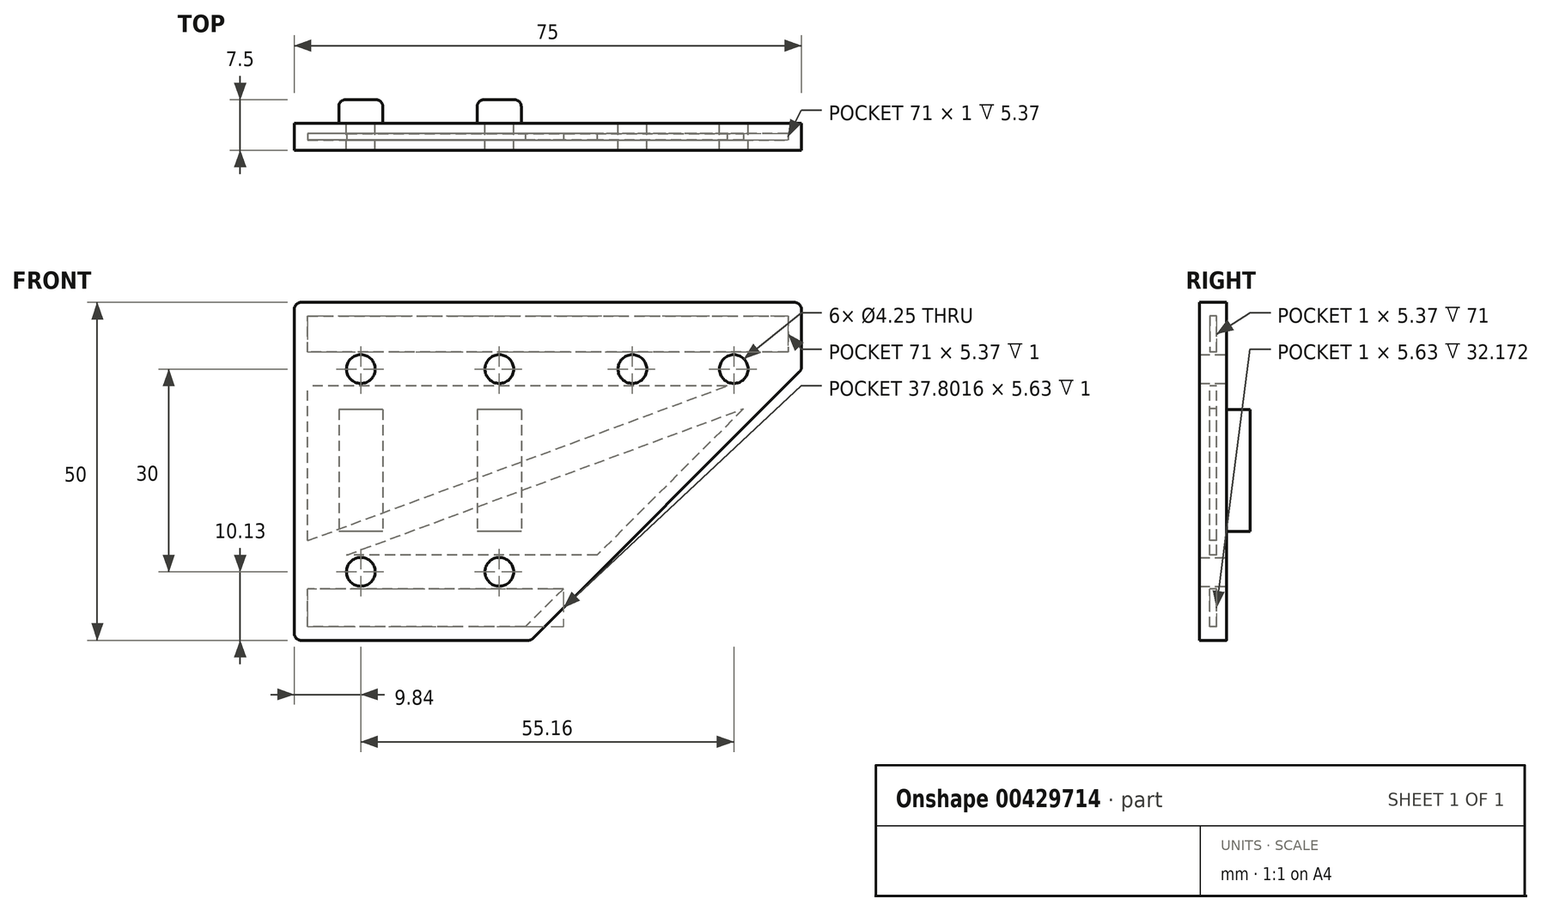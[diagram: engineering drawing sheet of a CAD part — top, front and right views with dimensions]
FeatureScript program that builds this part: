
annotation { "Feature Type Name" : "Feature", "Feature Type Description" : "" }
export const myFeature = defineFeature(function(context is Context, id is Id, definition is map)
    precondition{}
    {
        {
            var Q0;
            Q0=qCreatedBy(makeId("Front.planeOp"),FACE);
            var sketch = newSketch(context, id + "F0", { "sketchPlane" : qUnion([Q0])});
            skLineSegment(sketch, "E0", {"start": v(0, 0) * mm, "end": v(0, 50) * mm});
            skLineSegment(sketch, "E1", {"start": v(0, 50) * mm, "end": v(75, 50) * mm});
            skLineSegment(sketch, "E2", {"start": v(75, 50) * mm, "end": v(75, 40) * mm});
            skLineSegment(sketch, "E3", {"start": v(75, 40) * mm, "end": v(35, 0) * mm});
            skLineSegment(sketch, "E4", {"start": v(35, 0) * mm, "end": v(0, 0) * mm});
            skSolve(sketch);
        }
        {
            var Q0;
            Q0 = qSketchRegion(id + "F0", true);
            extrude(context, id + "F1", {"entities" : qUnion([Q0]), "depth" : 1.5 * mm});
        }
        {
            var Q0;
            Q0=makeQuery(id+"F1.opExtrude","CAP_FACE",FACE,{"disambiguationData":[OSD([sQuery(id+"F0.wireOp",EDGE,"E0"),sQuery(id+"F0.wireOp",EDGE,"E1"),sQuery(id+"F0.wireOp",EDGE,"E2"),sQuery(id+"F0.wireOp",EDGE,"E3"),sQuery(id+"F0.wireOp",EDGE,"E4")])],"isStart":true});
            var sketch = newSketch(context, id + "F2", { "sketchPlane" : qUnion([Q0])});
            skLineSegment(sketch, "E5", {"start": v(-73, 42.63) * mm, "end": v(-2, 42.63) * mm});
            skLineSegment(sketch, "E6", {"start": v(-64.02, 37.63) * mm, "end": v(-2, 37.63) * mm});
            skLineSegment(sketch, "E7.0", {"start": v(0, 50) * mm, "end": v(-75, 50) * mm});
            skLineSegment(sketch, "E8.0", {"start": v(0, 0) * mm, "end": v(0, 50) * mm});
            skLineSegment(sketch, "E9.0", {"start": v(-2, 2) * mm, "end": v(-2, 7.63) * mm});
            skLineSegment(sketch, "E9.1", {"start": v(-34.17, 2) * mm, "end": v(-2, 2) * mm});
            skLineSegment(sketch, "E9.2", {"start": v(-2, 48) * mm, "end": v(-73, 48) * mm});
            skLineSegment(sketch, "E9.3", {"start": v(-73, 48) * mm, "end": v(-73, 42.63) * mm});
            skLineSegment(sketch, "E9.4", {"start": v(-66.42, 34.25) * mm, "end": v(-44.8, 12.63) * mm});
            skLineSegment(sketch, "E10", {"start": v(-44.8, 12.63) * mm, "end": v(-7.78, 12.63) * mm});
            skLineSegment(sketch, "E11", {"start": v(-39.8, 7.63) * mm, "end": v(-2, 7.63) * mm});
            skLineSegment(sketch, "E12.trimOffspring", {"start": v(-2, 42.63) * mm, "end": v(-2, 48) * mm});
            skLineSegment(sketch, "E13.trimOffspring", {"start": v(-39.8, 7.63) * mm, "end": v(-34.17, 2) * mm});
            skLineSegment(sketch, "E14.trimOffspring", {"start": v(-2, 14.76) * mm, "end": v(-2, 37.63) * mm});
            skLineSegment(sketch, "E15", {"start": v(-2, 12.63) * mm, "end": v(-69.8, 37.63) * mm, "construction": true});
            skLineSegment(sketch, "E16.0", {"start": v(-2, 14.76) * mm, "end": v(-64.02, 37.63) * mm});
            skLineSegment(sketch, "E17.0", {"start": v(-7.78, 12.63) * mm, "end": v(-66.42, 34.25) * mm});
            skSolve(sketch);
        }
        {
            var Q0;
            Q0=makeQuery(id+"F2.imprint","IMPRINT",FACE,{"disambiguationData":[TD([[makeQuery(id+"F2.imprint","IMPRINT",EDGE,{"derivedFrom":sQuery(id+"F2.wireOp",EDGE,"E5")}),-1.0]])]});
            extrude(context, id + "F3", {"entities" : qUnion([Q0]), "operationType" : NewBodyOperationType.ADD, "depth" : 1 * mm});
        }
        {
            var Q0;
            Q0=makeQuery(id+"F3.opExtrude","CAP_FACE",FACE,{"disambiguationData":[OSD([sQuery(id+"F0.wireOp",EDGE,"E2"),sQuery(id+"F0.wireOp",EDGE,"E3"),sQuery(id+"F0.wireOp",EDGE,"E4"),sQuery(id+"F2.wireOp",EDGE,"E5"),sQuery(id+"F2.wireOp",EDGE,"E6"),sQuery(id+"F2.wireOp",EDGE,"E7.0"),sQuery(id+"F2.wireOp",EDGE,"E8.0"),sQuery(id+"F2.wireOp",EDGE,"E9.0"),sQuery(id+"F2.wireOp",EDGE,"E9.1"),sQuery(id+"F2.wireOp",EDGE,"E9.2"),sQuery(id+"F2.wireOp",EDGE,"E9.3"),sQuery(id+"F2.wireOp",EDGE,"E9.4"),sQuery(id+"F2.wireOp",EDGE,"E10"),sQuery(id+"F2.wireOp",EDGE,"E11"),sQuery(id+"F2.wireOp",EDGE,"E12.trimOffspring"),sQuery(id+"F2.wireOp",EDGE,"E13.trimOffspring"),sQuery(id+"F2.wireOp",EDGE,"E14.trimOffspring"),sQuery(id+"F2.wireOp",EDGE,"E16.0"),sQuery(id+"F2.wireOp",EDGE,"E17.0")])],"isStart":false});
            var sketch = newSketch(context, id + "F4", { "sketchPlane" : qUnion([Q0])});
            skLineSegment(sketch, "E18.0", {"start": v(0, 50) * mm, "end": v(-75, 50) * mm});
            skLineSegment(sketch, "E19.0", {"start": v(-75, 50) * mm, "end": v(-75, 40) * mm});
            skLineSegment(sketch, "E20.0", {"start": v(-75, 40) * mm, "end": v(-35, 0) * mm});
            skLineSegment(sketch, "E21.0", {"start": v(-35, 0) * mm, "end": v(0, 0) * mm});
            skLineSegment(sketch, "E22.0", {"start": v(0, 0) * mm, "end": v(0, 50) * mm});
            skSolve(sketch);
        }
        {
            var Q0;
            Q0 = qSketchRegion(id + "F4", true);
            extrude(context, id + "F5", {"entities" : qUnion([Q0]), "operationType" : NewBodyOperationType.ADD, "depth" : 1.5 * mm});
        }
        {
            var Q0;
            Q0=makeQuery(id+"F1.opExtrude","CAP_FACE",FACE,{"disambiguationData":[OSD([sQuery(id+"F0.wireOp",EDGE,"E0"),sQuery(id+"F0.wireOp",EDGE,"E1"),sQuery(id+"F0.wireOp",EDGE,"E2"),sQuery(id+"F0.wireOp",EDGE,"E3"),sQuery(id+"F0.wireOp",EDGE,"E4")])],"isStart":true});
            var sketch = newSketch(context, id + "F6", { "sketchPlane" : qUnion([Q0])});
            skLineSegment(sketch, "E23", {"start": v(-6.5, 50) * mm, "end": v(-6.5, 0) * mm, "construction": true});
            skLineSegment(sketch, "E24", {"start": v(-13.18, 50) * mm, "end": v(-13.18, 0) * mm, "construction": true});
            skCircle(sketch, "E25", {"center": v(-9.84, 40.13) * mm, "radius": 2.12 * mm});
            skCircle(sketch, "E26", {"center": v(-9.84, 10.13) * mm, "radius": 2.12 * mm});
            skCircle(sketch, "E27", {"center": v(-30.32, 40.13) * mm, "radius": 2.12 * mm});
            skCircle(sketch, "E28", {"center": v(-30.32, 10.13) * mm, "radius": 2.12 * mm});
            skCircle(sketch, "E29", {"center": v(-50, 40.13) * mm, "radius": 2.12 * mm});
            skCircle(sketch, "E30", {"center": v(-65, 40.13) * mm, "radius": 2.12 * mm});
            skLineSegment(sketch, "E31", {"start": v(-13.18, 40.13) * mm, "end": v(-6.5, 40.13) * mm, "construction": true});
            skLineSegment(sketch, "E32", {"start": v(-13.18, 43.2) * mm, "end": v(-49.26, 43.2) * mm, "construction": true});
            skLineSegment(sketch, "E33", {"start": v(-13.18, 40.13) * mm, "end": v(-39.87, 40.13) * mm, "construction": true});
            skLineSegment(sketch, "E34", {"start": v(-26.98, 40.13) * mm, "end": v(-26.98, 18.65) * mm, "construction": true});
            skLineSegment(sketch, "E35", {"start": v(-30.32, 40.13) * mm, "end": v(-30.32, 27.39) * mm, "construction": true});
            skSolve(sketch);
        }
        {
            var Q0;
            Q0 = qSketchRegion(id + "F6", true);
            extrude(context, id + "F7", {"entities" : qUnion([Q0]), "operationType" : NewBodyOperationType.REMOVE, "oppositeDirection" : true, "depth" : 25 * mm, "hasSecondDirection" : true, "secondDirectionOppositeDirection" : false, "secondDirectionDepth" : 25 * mm});
        }
        {
            var Q0;
            Q0=makeQuery(id+"F5.opExtrude","CAP_FACE",FACE,{"disambiguationData":[OSD([sQuery(id+"F4.wireOp",EDGE,"E18.0"),sQuery(id+"F4.wireOp",EDGE,"E19.0"),sQuery(id+"F4.wireOp",EDGE,"E20.0"),sQuery(id+"F4.wireOp",EDGE,"E21.0"),sQuery(id+"F4.wireOp",EDGE,"E22.0")])],"isStart":false});
            var sketch = newSketch(context, id + "F8", { "sketchPlane" : qUnion([Q0])});
            skLineSegment(sketch, "E36.bottom", {"start": v(-13.1, 34.13) * mm, "end": v(-6.6, 34.13) * mm});
            skLineSegment(sketch, "E36.top", {"start": v(-13.1, 16.13) * mm, "end": v(-6.6, 16.13) * mm});
            skLineSegment(sketch, "E36.left", {"start": v(-13.1, 34.13) * mm, "end": v(-13.1, 16.13) * mm});
            skLineSegment(sketch, "E36.right", {"start": v(-6.6, 34.13) * mm, "end": v(-6.6, 16.13) * mm});
            skLineSegment(sketch, "E37", {"start": v(-9.84, 34.13) * mm, "end": v(-9.84, 30.86) * mm, "construction": true});
            skPoint(sketch, "E37.endSnap0", {"position": v(-9.84, 34.13) * mm});
            skLineSegment(sketch, "E38", {"start": v(-9.84, 39.13) * mm, "end": v(-9.84, 34.13) * mm, "construction": true});
            skLineSegment(sketch, "E39", {"start": v(-9.84, 11.13) * mm, "end": v(-9.84, 16.13) * mm, "construction": true});
            skLineSegment(sketch, "E40.bottom", {"start": v(-33.57, 34.13) * mm, "end": v(-27.07, 34.13) * mm});
            skLineSegment(sketch, "E40.top", {"start": v(-33.57, 16.13) * mm, "end": v(-27.07, 16.13) * mm});
            skLineSegment(sketch, "E40.left", {"start": v(-33.57, 34.13) * mm, "end": v(-33.57, 16.13) * mm});
            skLineSegment(sketch, "E40.right", {"start": v(-27.07, 34.13) * mm, "end": v(-27.07, 16.13) * mm});
            skLineSegment(sketch, "E41", {"start": v(-30.32, 16.13) * mm, "end": v(-30.32, 17.83) * mm, "construction": true});
            skSolve(sketch);
        }
        {
            var Q0;
            Q0 = qSketchRegion(id + "F8", true);
            extrude(context, id + "F9", {"entities" : qUnion([Q0]), "operationType" : NewBodyOperationType.ADD, "depth" : 3.5 * mm});
        }
        {
            var Q0;
            Q0=makeQuery(id+"F9.opExtrude","CAP_EDGE",EDGE,{"disambiguationData":[OSD([sQuery(id+"F8.wireOp",EDGE,"E40.left")])],"isStart":false});
            var Q1;
            Q1=makeQuery(id+"F9.opExtrude","CAP_EDGE",EDGE,{"disambiguationData":[OSD([sQuery(id+"F8.wireOp",EDGE,"E40.right")])],"isStart":false});
            var Q2;
            Q2=makeQuery(id+"F9.opExtrude","CAP_EDGE",EDGE,{"disambiguationData":[OSD([sQuery(id+"F8.wireOp",EDGE,"E36.left")])],"isStart":false});
            var Q3;
            Q3=makeQuery(id+"F9.opExtrude","CAP_EDGE",EDGE,{"disambiguationData":[OSD([sQuery(id+"F8.wireOp",EDGE,"E36.right")])],"isStart":false});
            var Q4;
            Q4=makeQuery(id+"F1.opExtrude","SWEPT_EDGE",EDGE,{"disambiguationData":[OSD([sQuery(id+"F0.wireOp",EDGE,"E0"),sQuery(id+"F0.wireOp",EDGE,"E1")])]});
            var Q5;
            Q5=makeQuery(id+"F1.opExtrude","SWEPT_EDGE",EDGE,{"disambiguationData":[OSD([sQuery(id+"F0.wireOp",EDGE,"E0"),sQuery(id+"F0.wireOp",EDGE,"E4")])]});
            var Q6;
            Q6=makeQuery(id+"F1.opExtrude","SWEPT_EDGE",EDGE,{"disambiguationData":[OSD([sQuery(id+"F0.wireOp",EDGE,"E1"),sQuery(id+"F0.wireOp",EDGE,"E2")])]});
            var Q7;
            Q7=makeQuery(id+"F1.opExtrude","SWEPT_EDGE",EDGE,{"disambiguationData":[OSD([sQuery(id+"F0.wireOp",EDGE,"E2"),sQuery(id+"F0.wireOp",EDGE,"E3")])]});
            var Q8;
            Q8=makeQuery(id+"F1.opExtrude","SWEPT_EDGE",EDGE,{"disambiguationData":[OSD([sQuery(id+"F0.wireOp",EDGE,"E3"),sQuery(id+"F0.wireOp",EDGE,"E4")])]});
            fillet(context, id + "F10", {"entities" : qUnion([Q0, Q1, Q2, Q3, Q4, Q5, Q6, Q7, Q8]), "radius" : 1 * mm, "tangentPropagation" : true, "allowEdgeOverflow" : false});
        }
    });
